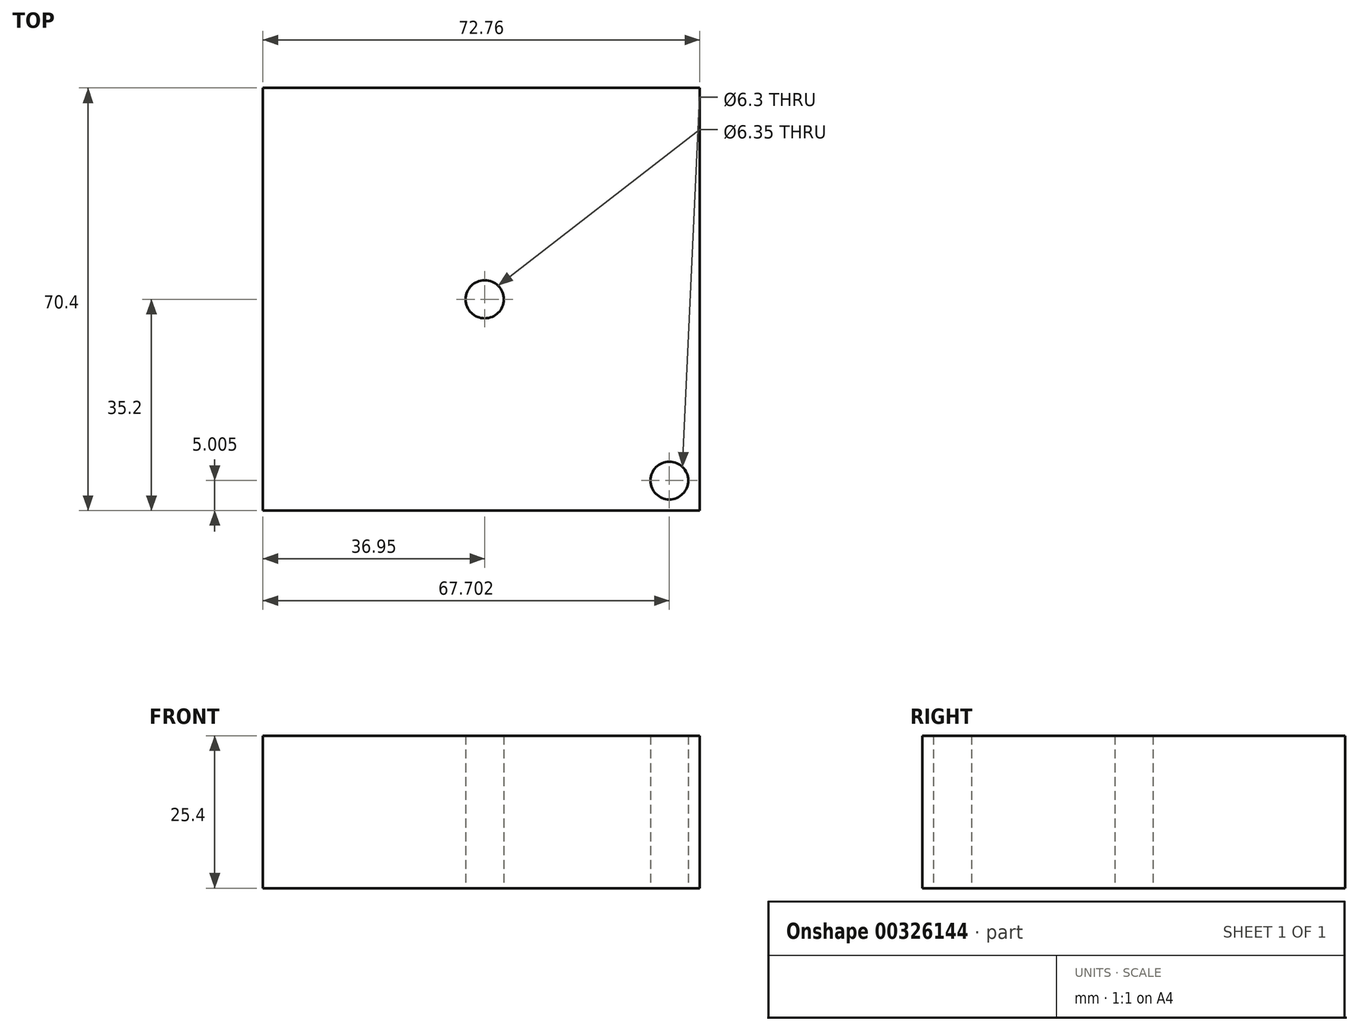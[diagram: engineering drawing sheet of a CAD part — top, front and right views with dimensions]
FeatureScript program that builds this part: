
annotation { "Feature Type Name" : "Feature", "Feature Type Description" : "" }
export const myFeature = defineFeature(function(context is Context, id is Id, definition is map)
    precondition{}
    {
        {
            var Q0;
            Q0=qCreatedBy(makeId("Top.planeOp"),FACE);
            var sketch = newSketch(context, id + "F0", { "sketchPlane" : qUnion([Q0])});
            skLineSegment(sketch, "E0.bottom", {"start": v(-36.95, 35.2) * mm, "end": v(35.8, 35.2) * mm});
            skLineSegment(sketch, "E0.top", {"start": v(-36.95, -35.2) * mm, "end": v(35.8, -35.2) * mm});
            skLineSegment(sketch, "E0.left", {"start": v(-36.95, 35.2) * mm, "end": v(-36.95, -35.2) * mm});
            skLineSegment(sketch, "E0.right", {"start": v(35.8, 35.2) * mm, "end": v(35.8, -35.2) * mm});
            skSolve(sketch);
        }
        {
            var Q0;
            Q0 = qSketchRegion(id + "F0", true);
            extrude(context, id + "F1", {"entities" : qUnion([Q0]), "depth" : 25.4 * mm});
        }
        {
            var Q0;
            Q0=qCreatedBy(makeId("Top.planeOp"),FACE);
            var sketch = newSketch(context, id + "F2", { "sketchPlane" : qUnion([Q0])});
            skCircle(sketch, "E1", {"center": v(30.75, -30.2) * mm, "radius": 3.15 * mm});
            skSolve(sketch);
        }
        {
            var Q0;
            Q0 = qSketchRegion(id + "F2", true);
            extrude(context, id + "F3", {"entities" : qUnion([Q0]), "depth" : 25.4 * mm});
        }
        {
            var Q0;
            Q0=makeQuery(id+"F3.opExtrude","SWEPT_BODY",BODY,{"disambiguationData":[OSD([sQuery(id+"F2.wireOp",EDGE,"E1")])]});
            var Q1;
            Q1=makeQuery(id+"F1.opExtrude","SWEPT_BODY",BODY,{"disambiguationData":[OSD([sQuery(id+"F0.wireOp",EDGE,"E0.bottom"),sQuery(id+"F0.wireOp",EDGE,"E0.top"),sQuery(id+"F0.wireOp",EDGE,"E0.left"),sQuery(id+"F0.wireOp",EDGE,"E0.right")])]});
            booleanBodies(context, id + "F4", {"operationType" : BooleanOperationType.SUBTRACTION, "tools" : qUnion([Q0]), "targets" : qUnion([Q1])});
        }
        {
            var Q0;
            Q0=qCreatedBy(makeId("Top.planeOp"),FACE);
            var sketch = newSketch(context, id + "F5", { "sketchPlane" : qUnion([Q0])});
            skPoint(sketch, "E2", {"position": v(0, 0) * mm});
            skSolve(sketch);
        }
        {
            var Q0;
            Q0=sQuery(id+"F5.wireOp",VERTEX,"E2");
            var Q1;
            Q1=makeQuery(id+"F1.opExtrude","SWEPT_BODY",BODY,{"disambiguationData":[OSD([sQuery(id+"F0.wireOp",EDGE,"E0.bottom"),sQuery(id+"F0.wireOp",EDGE,"E0.top"),sQuery(id+"F0.wireOp",EDGE,"E0.left"),sQuery(id+"F0.wireOp",EDGE,"E0.right")])]});
            hole(context, id + "F6", {"style" : HoleStyle.SIMPLE, "endStyle" : HoleEndStyle.THROUGH, "oppositeDirection" : true, "holeDiameter" : 6.35 * mm, "tappedDepth" : 12.7 * mm, "tapClearance" : 3, "startFromSketch" : true, "locations" : qUnion([Q0]), "scope" : qUnion([Q1])});
        }
    });
